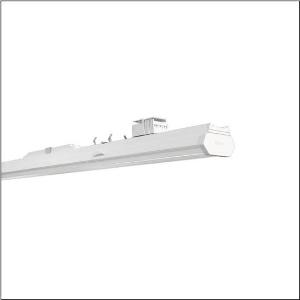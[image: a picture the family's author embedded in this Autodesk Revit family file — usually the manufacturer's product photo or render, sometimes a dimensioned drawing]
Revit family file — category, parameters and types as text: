
# Revit family: licross_r__21_protected_ho_52td1bdn4d5m_ff94
name_source: partatom
category: Lighting Fixtures
units: mm (PartAtom-declared; Revit-internal decimal feet)

## family parameters
Cut with Voids When Loaded = No
Host = Face
Light Source = No
Part Type = Normal
Room Calculation Point = No
Round Connector Dimension = Use Diameter
Shared = No

## types (1)
- --- (1 x LED, 13950 lm, 84.9 W, 4000K)
    Apparent Load = 85 VA
    CIE Flux Codes = 54 82 95 97 100
    Color Rendering = 80
    Color Temperature = 4000K
    Default Elevation = 1800 mm
    Description = Licross® 21 Protected HO, luminaire insert, of sheet steel, galvanised, coil coated, white, length: 1.500mm, width: 90mm, height: 103mm, LED rated luminous flux: 13.950lm, light colour: 840, control gear: DALI 2, with plug, 5-pole, with phase selection, mains connection: 220..240V, AC, 50/60Hz, rated input power: 85W, halogen-free wiring, primary optical cover: cover, of PMMA, light emission: direct distribution, primary light characteristic: symmetric, protection rating (complete): IP54, insulation class (complete): insulation class I (protective earthing), certification: CE, ENEC, VDE, UKCA, protection symbol: D if used in an environment with non-conductive dust loads with corresponding accessories, impact resistance: IK06, permissible ambient temperature for indoor applications: -25..+35°C, corresponds to IFS (International Featured Standards) requirements for safety and quality in the food industry, reducing of maximum allowable ambient temperature of 5°C with ceiling mounting, LABS conformity tested according to VDMA 24364:2018-05, packaging unit: 1 piece
    Height = 92 mm
    Lamp = 1 x LED
    Lamp Light Flux = 13950 lm
    Lamp Power = 84.9 W
    Lamp count = 1
    Length = 1500 mm
    Luminous efficacy = 164 lm/W
    Manufacturer = Siteco
    ModVariant = No
    Model = 52TD1BDN4D5M
    Mounting Place = Ceiling
    Mounting Type = Pendant
    Number of Poles = 1
    OnlyDefault = Yes
    Power Factor = 1
    Product Name = Licross® 21 Protected HO
    Product group = luminaire insert
    ProductGroupID = 901
    Protection Class = Protection class I
    Protection Degree = IP 54
    RLX_Detail_Level = 1
    RLX_Emergency_Light_Flux = 0 lm
    RLX_Emergency_Type = 0
    RLX_Emergency_Type_DB = No
    RlxData = <blob elided: 24329 chars, md5=40cba207>
    Socket = socket
    Standby Power = 0 W
    System Light Flux = 13950 lm
    System Power = 85 W
    Type Comments = factory setting: luminous flux: 100 % | dim-lin: 254 | 484 mA
    Type Image = l_1256148.jpg
    URL = http://relux.com
    VarID = @adj_060707
    Voltage = 0 V
    Weight = 0.00 kg
    Width = 88 mm

## geometry (parser evidence)
native form markers: Blend x4, Sweep x10
no freeform markers — native parametric forms only
